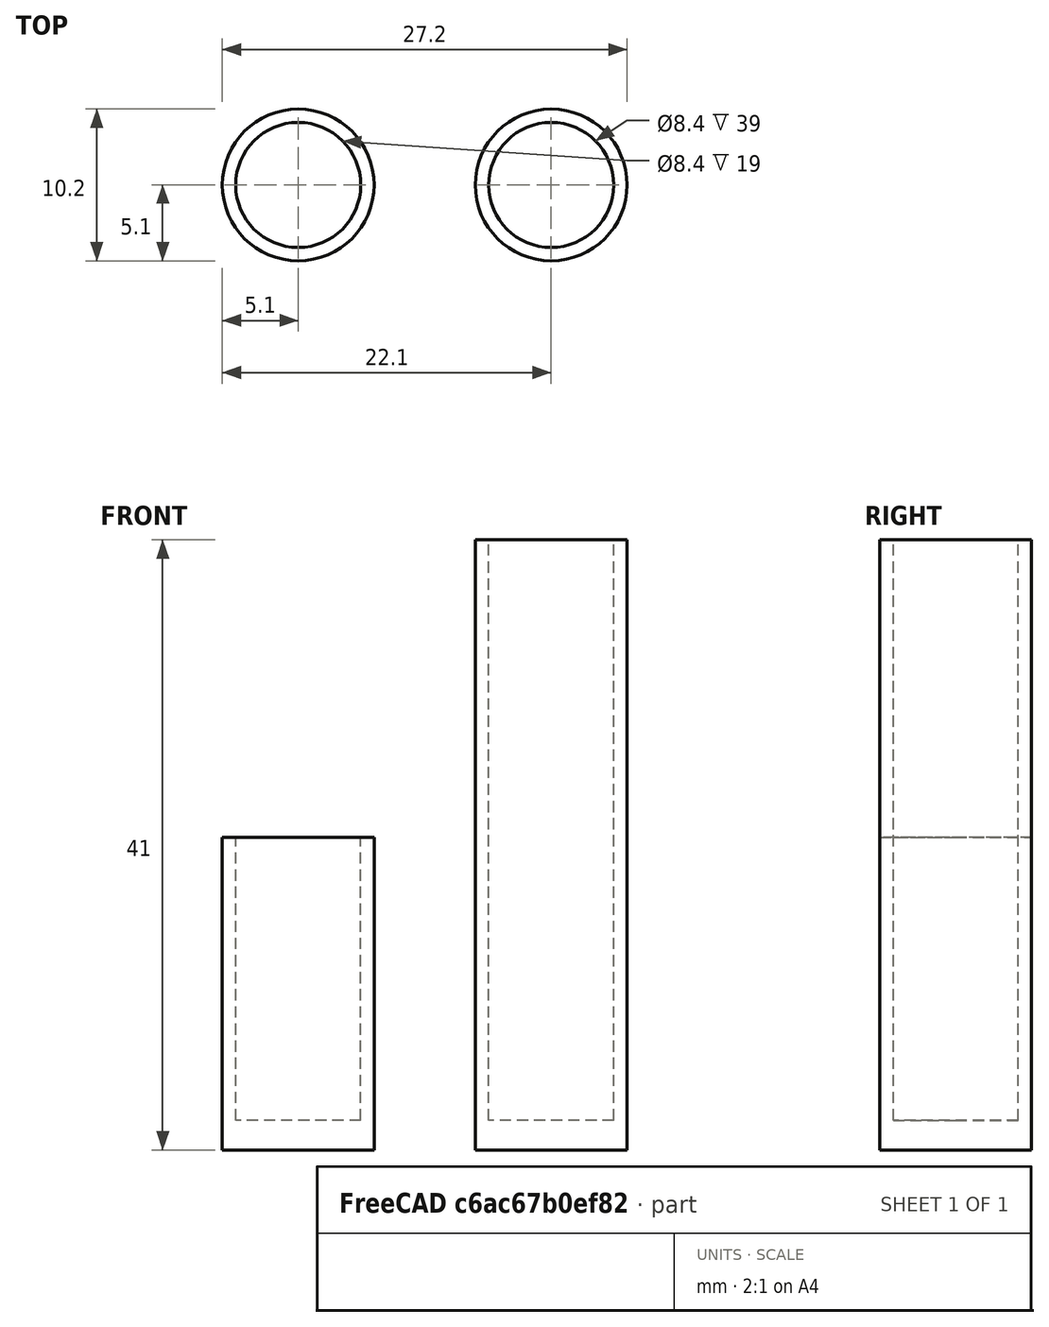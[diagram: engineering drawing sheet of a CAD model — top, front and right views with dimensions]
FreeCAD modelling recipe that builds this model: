
FCSTD DOCUMENT  (FreeCAD 0.18R14555 (Git shallow))
Label: rod-cutter-guide
License: All rights reserved
LicenseURL: http://en.wikipedia.org/wiki/All_rights_reserved
objects: Part::Cylinder×4, Part::Cut×2
note: 6 computed .brp shape members not serialized (recipe doc carries the construction recipe); baked Part::Feature solids carry a one-line shape summary decoded from their .brp

FEATURE [Part::Cylinder] Cylinder
  Angle = 360
  AttacherType = Attacher::AttachEngine3D
  Height = 39
  Placement = pos=(0,0,2) rot=(0,0,1;0rad)
  Radius = 4.2
FEATURE [Part::Cylinder] Cylinder001
  Angle = 360
  AttacherType = Attacher::AttachEngine3D
  Height = 41
  Radius = 5.1
FEATURE [Part::Cut] Cut  label="39mm"
  Base = -> Cylinder001
  Placement = pos=(17,0,0) rot=(0,0,1;0rad)
  Tool = -> Cylinder
FEATURE [Part::Cylinder] Cylinder002
  Angle = 360
  AttacherType = Attacher::AttachEngine3D
  Height = 19
  Placement = pos=(0,0,2) rot=(0,0,1;0rad)
  Radius = 4.2
FEATURE [Part::Cylinder] Cylinder003
  Angle = 360
  AttacherType = Attacher::AttachEngine3D
  Height = 21
  Radius = 5.1
FEATURE [Part::Cut] Cut001  label="19mm"
  Base = -> Cylinder003
  Tool = -> Cylinder002
